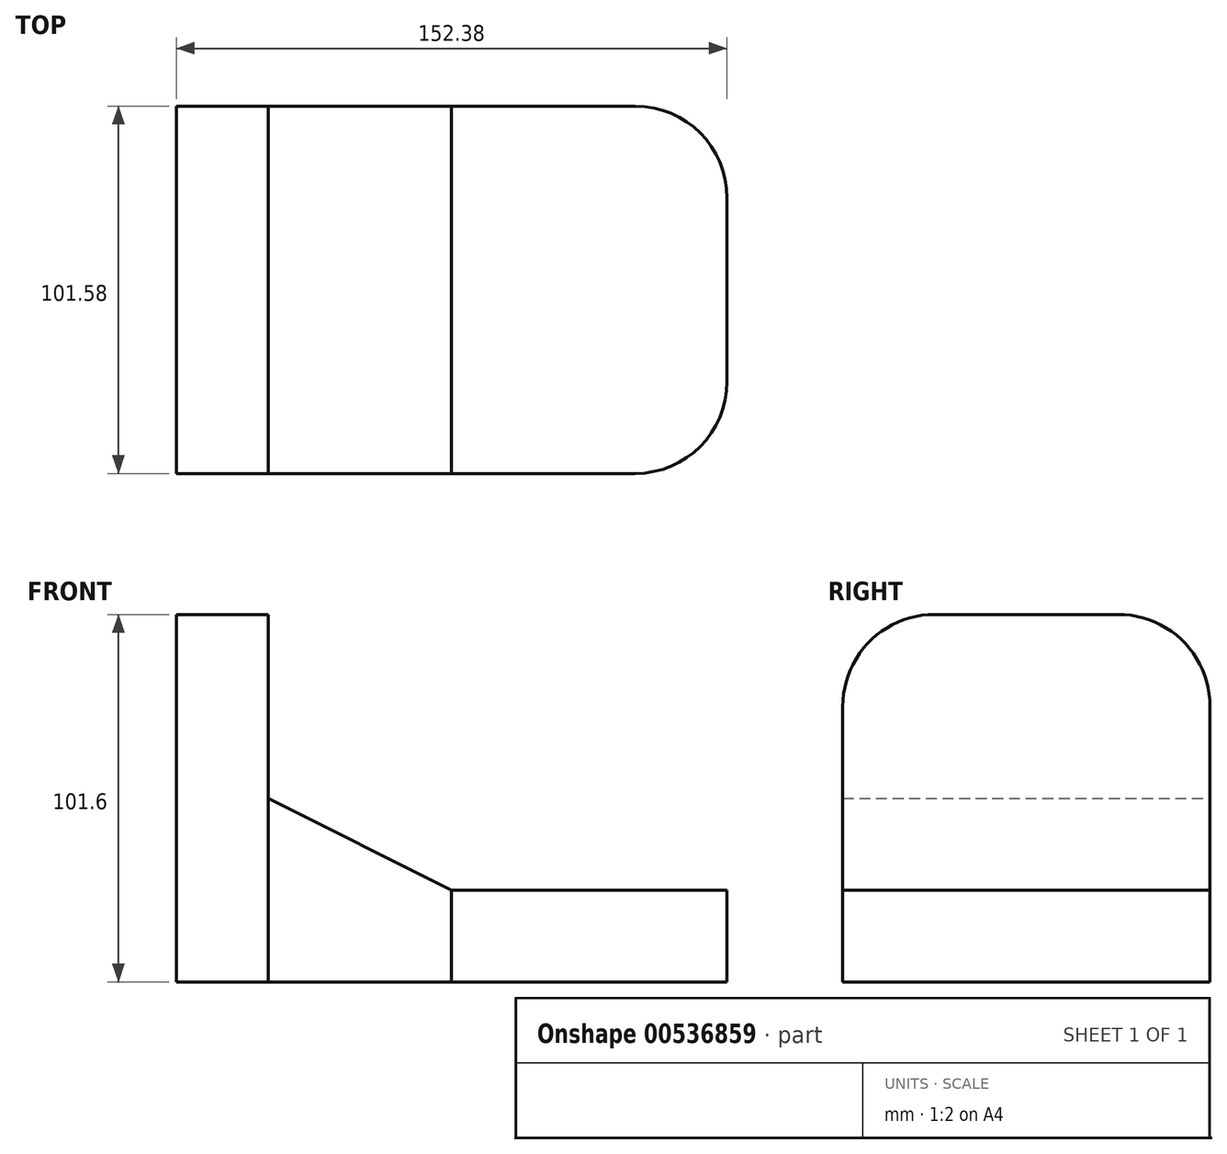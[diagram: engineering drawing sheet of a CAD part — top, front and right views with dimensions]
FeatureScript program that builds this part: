
annotation { "Feature Type Name" : "Feature", "Feature Type Description" : "" }
export const myFeature = defineFeature(function(context is Context, id is Id, definition is map)
    precondition{}
    {
        {
            var Q0;
            Q0=qCreatedBy(makeId("Top.planeOp"),FACE);
            var sketch = newSketch(context, id + "F0", { "sketchPlane" : qUnion([Q0])});
            skLineSegment(sketch, "E0.bottom", {"start": v(-25.4, -50.8) * mm, "end": v(25.4, -50.8) * mm});
            skLineSegment(sketch, "E0.top", {"start": v(-25.4, 50.8) * mm, "end": v(25.4, 50.8) * mm});
            skLineSegment(sketch, "E0.left", {"start": v(-25.4, -50.8) * mm, "end": v(-25.4, 50.8) * mm});
            skLineSegment(sketch, "E0.right", {"start": v(25.4, -50.8) * mm, "end": v(25.4, 50.8) * mm});
            skPoint(sketch, "E0.middle", {"position": v(0, 0) * mm});
            skLineSegment(sketch, "E1.bottom", {"start": v(-25.4, -50.8) * mm, "end": v(-50.8, -50.8) * mm});
            skLineSegment(sketch, "E1.top", {"start": v(-25.4, 50.8) * mm, "end": v(-50.8, 50.8) * mm});
            skLineSegment(sketch, "E1.right", {"start": v(-50.8, -50.8) * mm, "end": v(-50.8, 50.8) * mm});
            skLineSegment(sketch, "E2.bottom", {"start": v(25.4, 50.8) * mm, "end": v(76.19, 50.8) * mm});
            skLineSegment(sketch, "E2.top", {"start": v(25.4, -50.8) * mm, "end": v(76.19, -50.8) * mm});
            skLineSegment(sketch, "E2.left", {"start": v(25.4, 50.8) * mm, "end": v(25.4, -50.8) * mm});
            skLineSegment(sketch, "E2.right", {"start": v(101.59, 25.4) * mm, "end": v(101.59, -25.4) * mm});
            skPoint(sketch, "E3.visualSharp", {"position": v(101.59, 50.8) * mm});
            skArc(sketch, "E3.filletArc", {"start": v(101.59, 25.4) * mm, "mid": v(94.15, 43.35) * mm, "end": v(76.19, 50.8) * mm});
            skPoint(sketch, "E4.visualSharp", {"position": v(101.59, -50.8) * mm});
            skArc(sketch, "E4.filletArc", {"start": v(76.19, -50.8) * mm, "mid": v(94.15, -43.35) * mm, "end": v(101.59, -25.4) * mm});
            skSolve(sketch);
        }
        {
            var Q0;
            Q0=makeQuery(id+"F0.imprint","IMPRINT",FACE,{"disambiguationData":[TD([[makeQuery(id+"F0.imprint","IMPRINT",EDGE,{"derivedFrom":sQuery(id+"F0.wireOp",EDGE,"E1.bottom")}),-1.0]])]});
            extrude(context, id + "F1", {"entities" : qUnion([Q0]), "depth" : 101.6 * mm, "offsetDistance" : 25.4 * mm});
        }
        {
            var Q0;
            Q0=makeQuery(id+"F0.imprint","IMPRINT",FACE,{"disambiguationData":[TD([[makeQuery(id+"F0.imprint","IMPRINT",EDGE,{"derivedFrom":sQuery(id+"F0.wireOp",EDGE,"E0.bottom")}),1.0]])]});
            extrude(context, id + "F2", {"entities" : qUnion([Q0]), "operationType" : NewBodyOperationType.ADD, "depth" : 25.4 * mm, "offsetDistance" : 25.4 * mm});
        }
        {
            var Q0;
            Q0=makeQuery(id+"F0.imprint","IMPRINT",FACE,{"disambiguationData":[TD([[makeQuery(id+"F0.imprint","IMPRINT",EDGE,{"derivedFrom":sQuery(id+"F0.wireOp",EDGE,"E2.bottom")}),-1.0]])]});
            extrude(context, id + "F3", {"entities" : qUnion([Q0]), "operationType" : NewBodyOperationType.ADD, "depth" : 25.4 * mm, "offsetDistance" : 25.4 * mm});
        }
        {
            var Q0;
            Q0=makeQuery(id+"F0.imprint","IMPRINT",FACE,{"disambiguationData":[TD([[makeQuery(id+"F0.imprint","IMPRINT",EDGE,{"derivedFrom":sQuery(id+"F0.wireOp",EDGE,"E0.bottom")}),1.0]])]});
            extrude(context, id + "F4", {"entities" : qUnion([Q0]), "operationType" : NewBodyOperationType.ADD, "depth" : 50.8 * mm, "offsetDistance" : 25.4 * mm});
        }
        {
            var Q0;
            Q0=makeQuery(id+"F1.opExtrude","SWEPT_FACE",FACE,{"disambiguationData":[OSD([sQuery(id+"F0.wireOp",EDGE,"E1.right")])]});
            var sketch = newSketch(context, id + "F5", { "sketchPlane" : qUnion([Q0])});
            skLineSegment(sketch, "E5.bottom", {"start": v(-50.8, 0) * mm, "end": v(50.8, 0) * mm});
            skLineSegment(sketch, "E5.top", {"start": v(-25.4, 101.6) * mm, "end": v(25.4, 101.6) * mm});
            skLineSegment(sketch, "E5.left", {"start": v(-50.8, 0) * mm, "end": v(-50.8, 76.2) * mm});
            skLineSegment(sketch, "E5.right", {"start": v(50.8, 0) * mm, "end": v(50.8, 76.2) * mm});
            skPoint(sketch, "E6.visualSharp", {"position": v(-50.8, 101.6) * mm});
            skArc(sketch, "E6.filletArc", {"start": v(-25.4, 101.6) * mm, "mid": v(-43.35, 94.16) * mm, "end": v(-50.8, 76.2) * mm});
            skPoint(sketch, "E7.visualSharp", {"position": v(50.8, 101.6) * mm});
            skArc(sketch, "E7.filletArc", {"start": v(50.8, 76.2) * mm, "mid": v(43.35, 94.16) * mm, "end": v(25.4, 101.6) * mm});
            skSolve(sketch);
        }
        {
            var Q0;
            Q0 = qSketchRegion(id + "F5", true);
            extrude(context, id + "F6", {"entities" : qUnion([Q0]), "operationType" : NewBodyOperationType.INTERSECT, "oppositeDirection" : true, "depth" : 25.4 * mm, "offsetDistance" : 25.4 * mm});
        }
        {
            var Q0;
            Q0=makeQuery(id+"F0.imprint","IMPRINT",FACE,{"disambiguationData":[TD([[makeQuery(id+"F0.imprint","IMPRINT",EDGE,{"derivedFrom":sQuery(id+"F0.wireOp",EDGE,"E2.bottom")}),-1.0]])]});
            extrude(context, id + "F7", {"entities" : qUnion([Q0]), "depth" : 25.4 * mm, "offsetDistance" : 25.4 * mm});
        }
        {
            var Q0;
            Q0=makeQuery(id+"F0.imprint","IMPRINT",FACE,{"disambiguationData":[TD([[makeQuery(id+"F0.imprint","IMPRINT",EDGE,{"derivedFrom":sQuery(id+"F0.wireOp",EDGE,"E0.bottom")}),1.0]])]});
            extrude(context, id + "F8", {"entities" : qUnion([Q0]), "depth" : 50.8 * mm, "offsetDistance" : 25.4 * mm});
        }
        {
            var Q0;
            Q0=makeQuery(id+"F8.opExtrude","SWEPT_FACE",FACE,{"disambiguationData":[OSD([sQuery(id+"F0.wireOp",EDGE,"E0.bottom")])]});
            var sketch = newSketch(context, id + "F9", { "sketchPlane" : qUnion([Q0])});
            skLineSegment(sketch, "E8.bottom", {"start": v(25.4, 50.8) * mm, "end": v(-25.4, 50.8) * mm});
            skLineSegment(sketch, "E8.left", {"start": v(25.4, 50.8) * mm, "end": v(25.4, 25.4) * mm});
            skLineSegment(sketch, "E9", {"start": v(-25.4, 50.8) * mm, "end": v(25.4, 25.4) * mm});
            skSolve(sketch);
        }
        {
            var Q0;
            Q0=makeQuery(id+"F9.imprint","IMPRINT",FACE,{"disambiguationData":[TD([[makeQuery(id+"F9.imprint","IMPRINT",EDGE,{"derivedFrom":sQuery(id+"F9.wireOp",EDGE,"E8.bottom")}),-1.0]])]});
            extrude(context, id + "F10", {"entities" : qUnion([Q0]), "operationType" : NewBodyOperationType.REMOVE, "oppositeDirection" : true, "depth" : 105.16 * mm, "offsetDistance" : 25.4 * mm});
        }
    });
